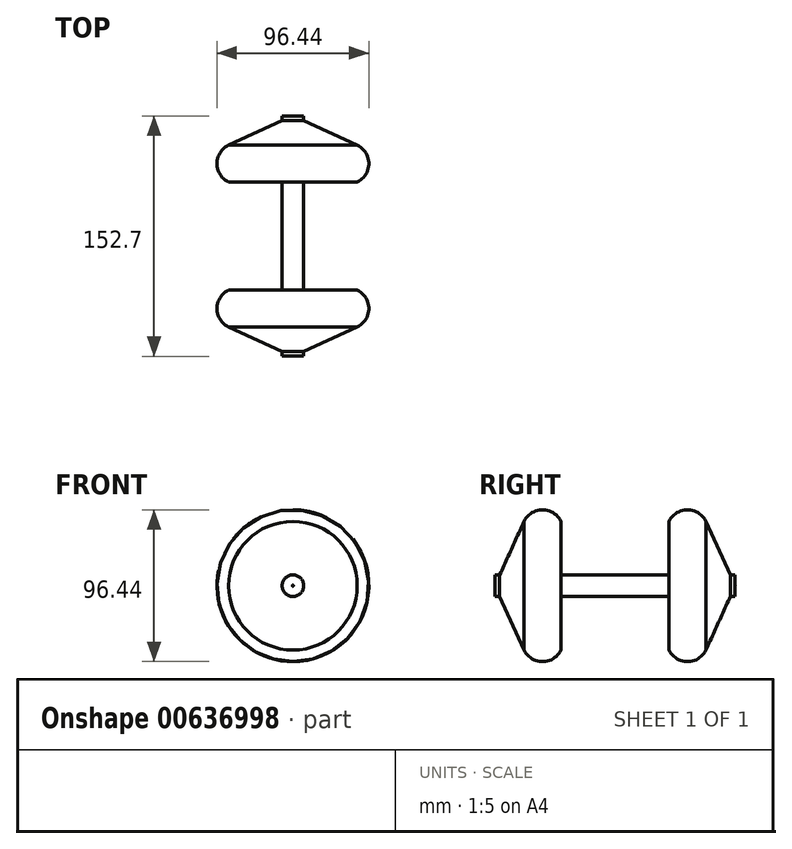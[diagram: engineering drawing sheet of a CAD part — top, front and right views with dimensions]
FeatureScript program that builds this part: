
annotation { "Feature Type Name" : "Feature", "Feature Type Description" : "" }
export const myFeature = defineFeature(function(context is Context, id is Id, definition is map)
    precondition{}
    {
        {
            var Q0;
            Q0=qCreatedBy(makeId("Front.planeOp"),FACE);
            var sketch = newSketch(context, id + "F0", { "sketchPlane" : qUnion([Q0])});
            skCircle(sketch, "E0", {"center": v(0, 0) * mm, "radius": 6.86 * mm});
            skSolve(sketch);
        }
        {
            var Q0;
            Q0=makeQuery(id+"F0.imprint","IMPRINT",FACE,{"disambiguationData":[TD([[makeQuery(id+"F0.imprint","IMPRINT",EDGE,{"derivedFrom":sQuery(id+"F0.wireOp",EDGE,"E0")}),1.0]])]});
            extrude(context, id + "F1", {"entities" : qUnion([Q0]), "depth" : 76.2 * mm, "offsetDistance" : 25.4 * mm, "hasSecondDirection" : true, "secondDirectionOppositeDirection" : true, "secondDirectionDepth" : 76.2 * mm});
        }
        {
            var Q0;
            Q0=qCreatedBy(makeId("Right.planeOp"),FACE);
            var sketch = newSketch(context, id + "F2", { "sketchPlane" : qUnion([Q0])});
            skLineSegment(sketch, "E1", {"start": v(0, 0) * mm, "end": v(-34.3, 0) * mm});
            skLineSegment(sketch, "E2", {"start": v(-34.3, 0) * mm, "end": v(-34.3, 40.84) * mm});
            skLineSegment(sketch, "E3", {"start": v(-57.76, 40.84) * mm, "end": v(-57.76, 0) * mm});
            skLineSegment(sketch, "E4", {"start": v(-57.76, 0) * mm, "end": v(-34.3, 0) * mm});
            skArc(sketch, "E5", {"start": v(-34.3, 40.84) * mm, "mid": v(-46.02, 48.22) * mm, "end": v(-57.76, 40.84) * mm});
            skLineSegment(sketch, "E6.MirrorCS", {"start": v(34.3, 0) * mm, "end": v(34.3, -40.84) * mm});
            skLineSegment(sketch, "E7.MirrorCS", {"start": v(57.76, -40.84) * mm, "end": v(57.76, 0) * mm});
            skArc(sketch, "E8.MirrorCS", {"start": v(34.3, -40.84) * mm, "mid": v(46.02, -48.22) * mm, "end": v(57.76, -40.84) * mm});
            skLineSegment(sketch, "E9.MirrorCS", {"start": v(57.76, 0) * mm, "end": v(34.3, 0) * mm});
            skPoint(sketch, "E10.MirrorCS.end.orphan", {"position": v(-34.3, -40.84) * mm});
            skPoint(sketch, "E10.MirrorCS.start.orphan", {"position": v(-34.3, 0) * mm});
            skPoint(sketch, "E11.MirrorCS.end.orphan", {"position": v(-57.76, 0) * mm});
            skPoint(sketch, "E11.MirrorCS.start.orphan", {"position": v(-57.76, -40.84) * mm});
            skLineSegment(sketch, "E12", {"start": v(76.35, 0) * mm, "end": v(57.76, -40.84) * mm});
            skLineSegment(sketch, "E13", {"start": v(76.35, 0) * mm, "end": v(57.76, 0) * mm});
            skLineSegment(sketch, "E14", {"start": v(-57.76, 40.84) * mm, "end": v(-76.35, 0) * mm});
            skLineSegment(sketch, "E15", {"start": v(-57.76, 0) * mm, "end": v(-76.35, 0) * mm});
            skSolve(sketch);
        }
        {
            var Q0;
            Q0=makeQuery(id+"F2.imprint","IMPRINT",FACE,{"disambiguationData":[TD([[makeQuery(id+"F2.imprint","IMPRINT",EDGE,{"derivedFrom":sQuery(id+"F2.wireOp",EDGE,"E2")}),1.0]])]});
            var Q1;
            Q1=sQuery(id+"F2.wireOp",EDGE,"E4");
            revolve(context, id + "F3", {"operationType" : NewBodyOperationType.ADD, "entities" : qUnion([Q0]), "axis" : qUnion([Q1]), "revolveType" : RevolveType.FULL});
        }
        {
            var Q0;
            Q0=makeQuery(id+"F2.imprint","IMPRINT",FACE,{"disambiguationData":[TD([[makeQuery(id+"F2.imprint","IMPRINT",EDGE,{"derivedFrom":sQuery(id+"F2.wireOp",EDGE,"E6.MirrorCS")}),1.0]])]});
            var Q1;
            Q1=sQuery(id+"F2.wireOp",EDGE,"E9.MirrorCS");
            revolve(context, id + "F4", {"operationType" : NewBodyOperationType.ADD, "entities" : qUnion([Q0]), "axis" : qUnion([Q1]), "revolveType" : RevolveType.FULL, "oppositeDirection" : true});
        }
        {
            var Q0;
            Q0=makeQuery(id+"F2.imprint","IMPRINT",FACE,{"disambiguationData":[TD([[makeQuery(id+"F2.imprint","IMPRINT",EDGE,{"derivedFrom":sQuery(id+"F2.wireOp",EDGE,"E7.MirrorCS")}),-1.0]])]});
            var Q1;
            Q1=sQuery(id+"F2.wireOp",EDGE,"E13");
            revolve(context, id + "F5", {"operationType" : NewBodyOperationType.ADD, "entities" : qUnion([Q0]), "axis" : qUnion([Q1]), "revolveType" : RevolveType.FULL});
        }
        {
            var Q0;
            Q0=makeQuery(id+"F2.imprint","IMPRINT",FACE,{"disambiguationData":[TD([[makeQuery(id+"F2.imprint","IMPRINT",EDGE,{"derivedFrom":sQuery(id+"F2.wireOp",EDGE,"E3")}),-1.0]])]});
            var Q1;
            Q1=sQuery(id+"F2.wireOp",EDGE,"E15");
            revolve(context, id + "F6", {"operationType" : NewBodyOperationType.ADD, "entities" : qUnion([Q0]), "axis" : qUnion([Q1]), "revolveType" : RevolveType.FULL});
        }
    });
